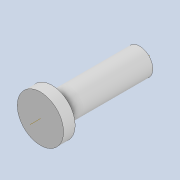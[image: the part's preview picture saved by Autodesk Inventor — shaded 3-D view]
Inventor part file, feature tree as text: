
AUTODESK INVENTOR PART (.ipt)
format: ipt  version: 2021 (Build 250183000, 183)  size: 84,480 bytes
history: native  units: mm
features: revolve x1, sketch x1
ambient origin geometry x8: Origin, YZ Plane, XZ Plane, XY Plane, X Axis, Y Axis, Z Axis, Center Point
bodies: Solid1 (feature_tree)
feature tree (2):
  revolve  "Revolution1"  [1 undecoded]
  sketch  "Sketch1"  dims[d0=3.5mm d1=4.0mm d2=30.0mm d3=7.0mm d4=90.0deg]
note: 1 required parameter value undecoded (feature->parameter linkage not recoverable at this tier; creation-order binding heuristic only, values carry confidence <= 0.55)
